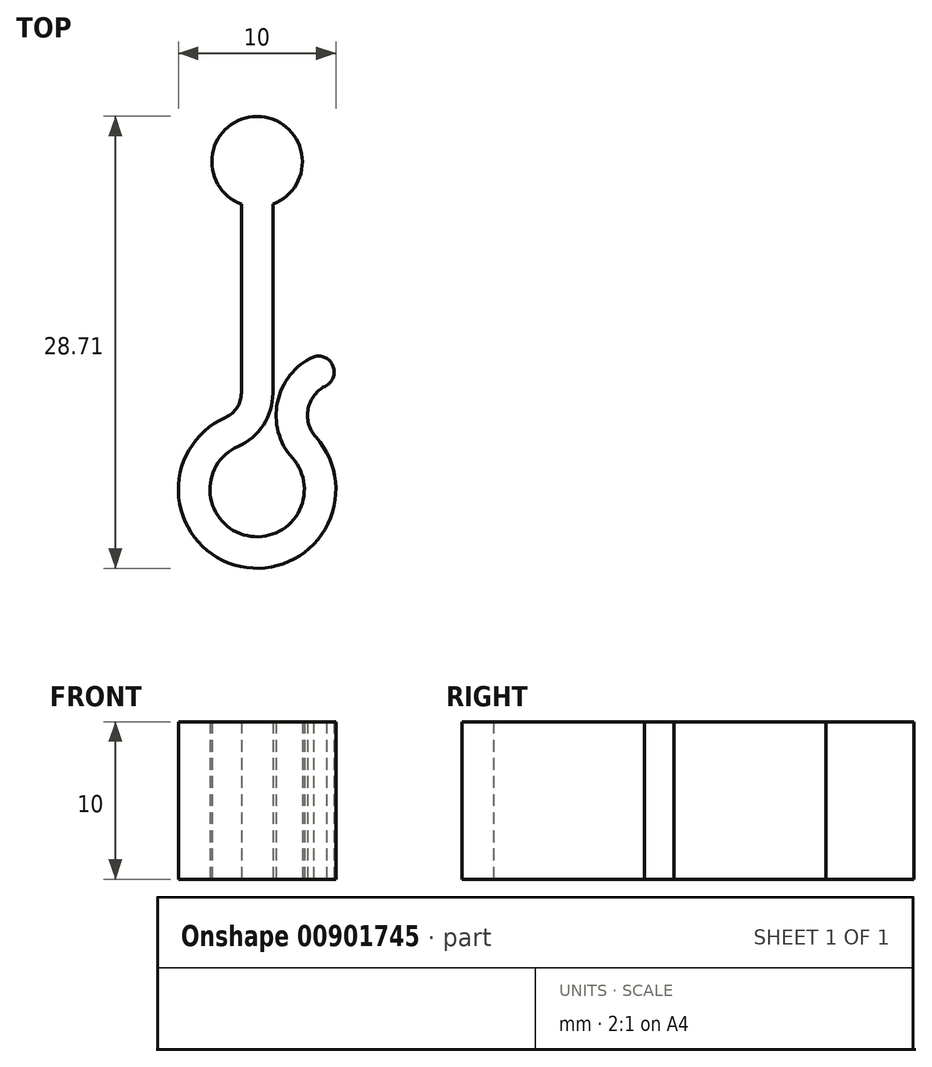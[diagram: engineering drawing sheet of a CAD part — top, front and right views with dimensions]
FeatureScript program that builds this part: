
annotation { "Feature Type Name" : "Feature", "Feature Type Description" : "" }
export const myFeature = defineFeature(function(context is Context, id is Id, definition is map)
    precondition{}
    {
        {
            var Q0;
            Q0=qCreatedBy(makeId("Top.planeOp"),FACE);
            var sketch = newSketch(context, id + "F0", { "sketchPlane" : qUnion([Q0])});
            skCircle(sketch, "E0", {"center": v(0, 0) * mm, "radius": 2.88 * mm});
            skLineSegment(sketch, "E1", {"start": v(-1, -2.7) * mm, "end": v(-1, -14.7) * mm});
            skLineSegment(sketch, "E2", {"start": v(1, -2.7) * mm, "end": v(1, -14.7) * mm});
            skArc(sketch, "E3", {"start": v(-2.02, -16.25) * mm, "mid": v(-1.28, -15.63) * mm, "end": v(-1, -14.7) * mm});
            skArc(sketch, "E4", {"start": v(-2.02, -16.25) * mm, "mid": v(-1.06, -25.71) * mm, "end": v(3.74, -17.5) * mm});
            skArc(sketch, "E5", {"start": v(4.42, -14.21) * mm, "mid": v(3.25, -15.69) * mm, "end": v(3.74, -17.5) * mm});
            skArc(sketch, "E6.0", {"start": v(-1.2, -18.08) * mm, "mid": v(0.4, -16.72) * mm, "end": v(1, -14.7) * mm});
            skArc(sketch, "E6.1", {"start": v(-1.2, -18.08) * mm, "mid": v(-0.64, -23.76) * mm, "end": v(2.24, -18.83) * mm});
            skArc(sketch, "E6.2", {"start": v(3.58, -12.4) * mm, "mid": v(1.3, -15.28) * mm, "end": v(2.24, -18.83) * mm});
            skArc(sketch, "E7", {"start": v(4.42, -14.21) * mm, "mid": v(4.8, -12.94) * mm, "end": v(3.58, -12.4) * mm});
            skSolve(sketch);
        }
        {
            var Q0;
            {var subQ0=sQuery(id+"F0.wireOp",EDGE,"E0");var subQ1=makeQuery(id+"F0.imprint","INTERSECT",VERTEX,{"derivedFrom":[subQ0,sQuery(id+"F0.wireOp",EDGE,"E1")]});Q0=makeQuery(id+"F0.imprint","IMPRINT",FACE,{"disambiguationData":[TD([[makeQuery(id+"F0.imprint","IMPRINT",EDGE,{"disambiguationData":[TD([[subQ1,-1.0]])],"derivedFrom":subQ0}),1.0]])]});}
            var Q1;
            {var subQ1=sQuery(id+"F0.wireOp",EDGE,"E1");Q1=makeQuery(id+"F0.imprint","IMPRINT",FACE,{"disambiguationData":[TD([[makeQuery(id+"F0.imprint","IMPRINT",EDGE,{"derivedFrom":subQ1}),1.0]])]});}
            extrude(context, id + "F1", {"entities" : qUnion([Q0, Q1]), "depth" : 10 * mm, "offsetDistance" : 25 * mm});
        }
    });
